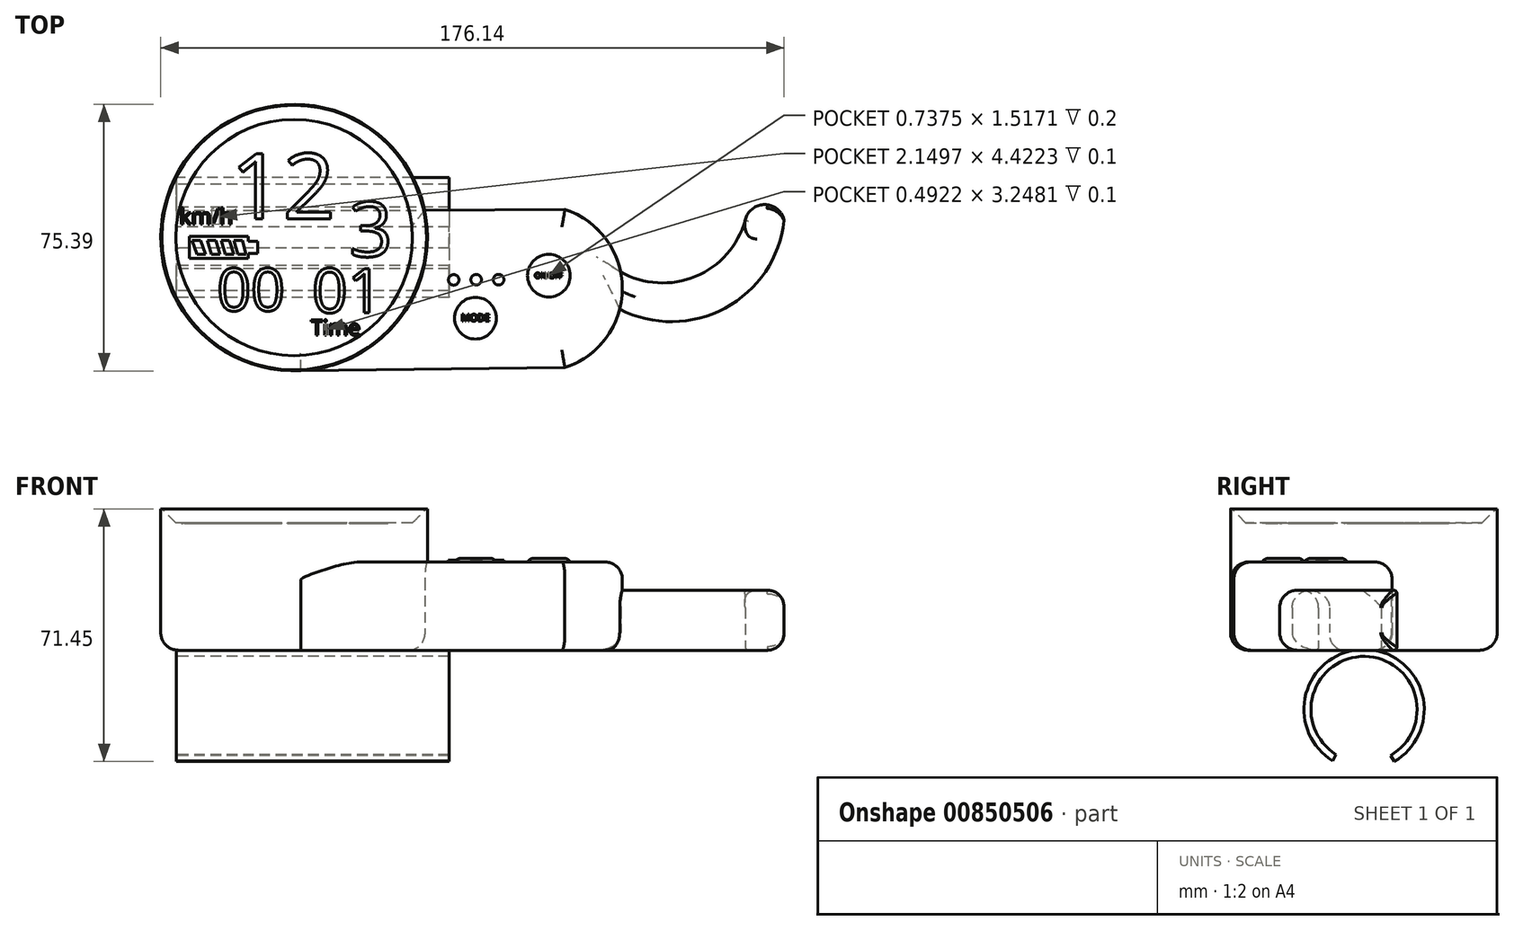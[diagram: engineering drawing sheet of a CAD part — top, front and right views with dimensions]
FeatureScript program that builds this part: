
annotation { "Feature Type Name" : "Feature", "Feature Type Description" : "" }
export const myFeature = defineFeature(function(context is Context, id is Id, definition is map)
    precondition{}
    {
        {
            var Q0;
            Q0=qCreatedBy(makeId("Top.planeOp"),FACE);
            var sketch = newSketch(context, id + "F0", { "sketchPlane" : qUnion([Q0])});
            skCircle(sketch, "E0", {"center": v(-18.77, 14.41) * mm, "radius": 37.7 * mm});
            skLineSegment(sketch, "E1", {"start": v(18.12, 22.13) * mm, "end": v(57.74, 22.38) * mm});
            skLineSegment(sketch, "E2.MirrorCS", {"start": v(-16.84, -23.23) * mm, "end": v(57.74, -22.38) * mm});
            skArc(sketch, "E3", {"start": v(57.74, -22.38) * mm, "mid": v(73.97, 0) * mm, "end": v(57.74, 22.38) * mm});
            skArc(sketch, "E4", {"start": v(73.5, 4.7) * mm, "mid": v(94.66, 3.43) * mm, "end": v(108.69, 19.33) * mm});
            skArc(sketch, "E5", {"start": v(73.23, -5.85) * mm, "mid": v(103.1, -5.5) * mm, "end": v(119.68, 19.33) * mm});
            skArc(sketch, "E6", {"start": v(119.68, 19.33) * mm, "mid": v(114.19, 23.75) * mm, "end": v(108.69, 19.33) * mm});
            skCircle(sketch, "E7", {"center": v(-18.77, 14.41) * mm, "radius": 32.4 * mm});
            skSolve(sketch);
        }
        {
            var Q0;
            {var subQ0=sQuery(id+"F0.wireOp",EDGE,"E0");var subQ1=makeQuery(id+"F0.imprint","INTERSECT",VERTEX,{"derivedFrom":[subQ0,sQuery(id+"F0.wireOp",EDGE,"E1")]});Q0=makeQuery(id+"F0.imprint","IMPRINT",FACE,{"disambiguationData":[TD([[makeQuery(id+"F0.imprint","IMPRINT",EDGE,{"disambiguationData":[TD([[subQ1,-1.0]])],"derivedFrom":subQ0}),1.0]])]});}
            extrude(context, id + "F1", {"entities" : qUnion([Q0]), "depth" : 40 * mm, "offsetDistance" : 25 * mm});
        }
        {
            var Q0;
            {var subQ3=sQuery(id+"F0.wireOp",EDGE,"E1");Q0=makeQuery(id+"F0.imprint","IMPRINT",FACE,{"disambiguationData":[TD([[makeQuery(id+"F0.imprint","IMPRINT",EDGE,{"derivedFrom":subQ3}),-1.0]])]});}
            extrude(context, id + "F2", {"entities" : qUnion([Q0]), "operationType" : NewBodyOperationType.ADD, "depth" : 25 * mm, "offsetDistance" : 25 * mm});
        }
        {
            var Q0;
            {var subQ0=sQuery(id+"F0.wireOp",EDGE,"E4");Q0=makeQuery(id+"F0.imprint","IMPRINT",FACE,{"disambiguationData":[TD([[makeQuery(id+"F0.imprint","IMPRINT",EDGE,{"derivedFrom":subQ0}),-1.0]])]});}
            extrude(context, id + "F3", {"entities" : qUnion([Q0]), "operationType" : NewBodyOperationType.ADD, "depth" : 17 * mm, "offsetDistance" : 25 * mm});
        }
        {
            var Q0;
            Q0=makeQuery(id+"F3.opExtrude","CAP_EDGE",EDGE,{"disambiguationData":[OSD([sQuery(id+"F0.wireOp",EDGE,"E5")])],"isStart":true});
            var Q1;
            Q1=makeQuery(id+"F3.opExtrude","CAP_EDGE",EDGE,{"disambiguationData":[OSD([sQuery(id+"F0.wireOp",EDGE,"E4")])],"isStart":false});
            var Q2;
            Q2=makeQuery(id+"F3.opExtrude","CAP_EDGE",EDGE,{"disambiguationData":[OSD([sQuery(id+"F0.wireOp",EDGE,"E5")])],"isStart":false});
            fillet(context, id + "F4", {"entities" : qUnion([Q0, Q1, Q2]), "radius" : 5 * mm, "tangentPropagation" : true, "allowEdgeOverflow" : false});
        }
        {
            var Q0;
            Q0=makeQuery(id+"F3.opExtrude","CAP_EDGE",EDGE,{"disambiguationData":[OSD([sQuery(id+"F0.wireOp",EDGE,"E6")])],"isStart":false});
            var Q1;
            Q1=makeQuery(id+"F4.opFillet","BLEND_EDGE",EDGE,{"blendedFrom":[makeQuery(id+"F3.opExtrude","CAP_EDGE",EDGE,{"disambiguationData":[OSD([sQuery(id+"F0.wireOp",EDGE,"E5")])],"isStart":false}),makeQuery(id+"F3.opExtrude","SWEPT_FACE",FACE,{"disambiguationData":[OSD([sQuery(id+"F0.wireOp",EDGE,"E6")])]})],"blendedInto":[makeQuery(id+"F3.opExtrude","SWEPT_FACE",FACE,{"disambiguationData":[OSD([sQuery(id+"F0.wireOp",EDGE,"E6")])]})]});
            fillet(context, id + "F5", {"entities" : qUnion([Q0, Q1]), "radius" : 1 * mm, "tangentPropagation" : true, "allowEdgeOverflow" : false});
        }
        {
            var Q0;
            Q0=makeQuery(id+"F2.opExtrude","CAP_EDGE",EDGE,{"disambiguationData":[OSD([sQuery(id+"F0.wireOp",EDGE,"E2.MirrorCS")])],"isStart":false});
            var Q1;
            Q1=makeQuery(id+"F2.opExtrude","CAP_EDGE",EDGE,{"disambiguationData":[OSD([sQuery(id+"F0.wireOp",EDGE,"E1")])],"isStart":false});
            var Q2;
            Q2=makeQuery(id+"F2.opExtrude","CAP_EDGE",EDGE,{"disambiguationData":[OSD([sQuery(id+"F0.wireOp",EDGE,"E2.MirrorCS")])],"isStart":true});
            var Q3;
            Q3=makeQuery(id+"F2.opExtrude","CAP_EDGE",EDGE,{"disambiguationData":[OSD([sQuery(id+"F0.wireOp",EDGE,"E1")])],"isStart":true});
            var Q4;
            {var subQ0=sQuery(id+"F0.wireOp",EDGE,"E1");var subQ1=sQuery(id+"F0.wireOp",EDGE,"E3");Q4=makeQuery(id+"F3.boolean.opBoolean","SPLIT",EDGE,{"disambiguationData":[TD([makeQuery(id+"F2.opExtrude","SWEPT_FACE",FACE,{"disambiguationData":[OSD([subQ0])]})])],"derivedFrom":makeQuery(id+"F2.opExtrude","CAP_EDGE",EDGE,{"disambiguationData":[OSD([subQ1])],"isStart":true})});}
            var Q5;
            {var subQ0=sQuery(id+"F0.wireOp",EDGE,"E2.MirrorCS");var subQ1=sQuery(id+"F0.wireOp",EDGE,"E3");Q5=makeQuery(id+"F3.boolean.opBoolean","SPLIT",EDGE,{"disambiguationData":[TD([makeQuery(id+"F2.opExtrude","SWEPT_FACE",FACE,{"disambiguationData":[OSD([subQ0])]})])],"derivedFrom":makeQuery(id+"F2.opExtrude","CAP_EDGE",EDGE,{"disambiguationData":[OSD([subQ1])],"isStart":true})});}
            var Q6;
            Q6=makeQuery(id+"F2.opExtrude","CAP_EDGE",EDGE,{"disambiguationData":[OSD([sQuery(id+"F0.wireOp",EDGE,"E3")])],"isStart":false});
            fillet(context, id + "F6", {"entities" : qUnion([Q0, Q1, Q2, Q3, Q4, Q5, Q6]), "radius" : 5 * mm, "tangentPropagation" : true, "allowEdgeOverflow" : false});
        }
        {
            var Q0;
            Q0=makeQuery(id+"F0.imprint","IMPRINT",FACE,{"disambiguationData":[TD([[makeQuery(id+"F0.imprint","IMPRINT",EDGE,{"derivedFrom":sQuery(id+"F0.wireOp",EDGE,"E7")}),1.0]])]});
            extrude(context, id + "F7", {"entities" : qUnion([Q0]), "operationType" : NewBodyOperationType.ADD, "depth" : 36 * mm, "offsetDistance" : 25 * mm});
        }
        {
            var Q0;
            Q0=makeQuery(id+"F1.opExtrude","CAP_EDGE",EDGE,{"disambiguationData":[OSD([sQuery(id+"F0.wireOp",EDGE,"E7")])],"isStart":false});
            chamfer(context, id + "F8", {"entities" : qUnion([Q0]), "width" : 5 * mm, "tangentPropagation" : true});
        }
        {
            var Q0;
            Q0=makeQuery(id+"F2.opExtrude","CAP_FACE",FACE,{"disambiguationData":[OSD([sQuery(id+"F0.wireOp",EDGE,"E0"),sQuery(id+"F0.wireOp",EDGE,"E1"),sQuery(id+"F0.wireOp",EDGE,"E2.MirrorCS"),sQuery(id+"F0.wireOp",EDGE,"E3")])],"isStart":false});
            var sketch = newSketch(context, id + "F9", { "sketchPlane" : qUnion([Q0])});
            skCircle(sketch, "E8", {"center": v(53.21, 3.66) * mm, "radius": 6.03 * mm});
            skCircle(sketch, "E9", {"center": v(32.47, -8.4) * mm, "radius": 5.9 * mm});
            skCircle(sketch, "E10", {"center": v(26.31, 2.45) * mm, "radius": 1.5 * mm});
            skCircle(sketch, "E11", {"center": v(32.67, 2.5) * mm, "radius": 1.5 * mm});
            skCircle(sketch, "E12", {"center": v(39, 2.52) * mm, "radius": 1.5 * mm});
            skSolve(sketch);
        }
        {
            var Q0;
            Q0=makeQuery(id+"F9.imprint","IMPRINT",FACE,{"disambiguationData":[TD([[makeQuery(id+"F9.imprint","IMPRINT",EDGE,{"derivedFrom":sQuery(id+"F9.wireOp",EDGE,"E9")}),1.0]])]});
            var Q1;
            Q1=makeQuery(id+"F9.imprint","IMPRINT",FACE,{"disambiguationData":[TD([[makeQuery(id+"F9.imprint","IMPRINT",EDGE,{"derivedFrom":sQuery(id+"F9.wireOp",EDGE,"E8")}),1.0]])]});
            extrude(context, id + "F10", {"entities" : qUnion([Q0, Q1]), "operationType" : NewBodyOperationType.ADD, "depth" : 1 * mm, "offsetDistance" : 25 * mm});
        }
        {
            var Q0;
            Q0=makeQuery(id+"F10.opExtrude","CAP_FACE",FACE,{"disambiguationData":[OSD([sQuery(id+"F9.wireOp",EDGE,"E9")])],"isStart":false});
            var Q1;
            Q1=makeQuery(id+"F10.opExtrude","CAP_FACE",FACE,{"disambiguationData":[OSD([sQuery(id+"F9.wireOp",EDGE,"E8")])],"isStart":false});
            fillet(context, id + "F11", {"entities" : qUnion([Q0, Q1]), "radius" : 2 * mm, "tangentPropagation" : true, "allowEdgeOverflow" : false});
        }
        {
            var Q0;
            Q0=makeQuery(id+"F9.imprint","IMPRINT",FACE,{"disambiguationData":[TD([[makeQuery(id+"F9.imprint","IMPRINT",EDGE,{"derivedFrom":sQuery(id+"F9.wireOp",EDGE,"E10")}),1.0]])]});
            var Q1;
            Q1=makeQuery(id+"F9.imprint","IMPRINT",FACE,{"disambiguationData":[TD([[makeQuery(id+"F9.imprint","IMPRINT",EDGE,{"derivedFrom":sQuery(id+"F9.wireOp",EDGE,"E11")}),1.0]])]});
            var Q2;
            Q2=makeQuery(id+"F9.imprint","IMPRINT",FACE,{"disambiguationData":[TD([[makeQuery(id+"F9.imprint","IMPRINT",EDGE,{"derivedFrom":sQuery(id+"F9.wireOp",EDGE,"E12")}),1.0]])]});
            extrude(context, id + "F12", {"entities" : qUnion([Q0, Q1, Q2]), "depth" : 0.5 * mm, "offsetDistance" : 25 * mm});
        }
        {
            var Q0;
            Q0=makeQuery(id+"F10.opExtrude","CAP_FACE",FACE,{"disambiguationData":[OSD([sQuery(id+"F9.wireOp",EDGE,"E9")])],"isStart":false});
            var sketch = newSketch(context, id + "F13", { "sketchPlane" : qUnion([Q0])});
            skText(sketch, "E13", { "text": "MODE", "fontName": "OpenSans-Regular.ttf"});
            skText(sketch, "E14", { "text": "ON/OFF", "fontName": "OpenSans-Regular.ttf"});
            const initialGuessF13  = {"E13": [0.02846, -0.00922, 1, 0, 0.00196], "E14": [0.0492, 0.00292, 1, 0, 0.00153]};
            skSetInitialGuess(sketch, initialGuessF13);
            skSolve(sketch);
        }
        {
            var Q0;
            Q0 = qSketchRegion(id + "F13", true);
            extrude(context, id + "F14", {"entities" : qUnion([Q0]), "operationType" : NewBodyOperationType.REMOVE, "oppositeDirection" : true, "depth" : 0.2 * mm, "offsetDistance" : 25 * mm});
        }
        {
            var Q0;
            Q0=makeQuery(id+"F1.opExtrude","CAP_EDGE",EDGE,{"disambiguationData":[OSD([sQuery(id+"F0.wireOp",EDGE,"E0")])],"isStart":true});
            fillet(context, id + "F15", {"entities" : qUnion([Q0]), "radius" : 5 * mm, "tangentPropagation" : true, "allowEdgeOverflow" : false});
        }
        {
            var Q0;
            Q0=makeQuery(id+"F7.opExtrude","CAP_FACE",FACE,{"disambiguationData":[OSD([sQuery(id+"F0.wireOp",EDGE,"E7")])],"isStart":false});
            var sketch = newSketch(context, id + "F16", { "sketchPlane" : qUnion([Q0])});
            skText(sketch, "E15", { "text": "12", "fontName": "OpenSans-Regular.ttf"});
            skText(sketch, "E16", { "text": "3", "fontName": "OpenSans-Regular.ttf"});
            skText(sketch, "E17", { "text": "01", "fontName": "OpenSans-Regular.ttf"});
            skText(sketch, "E18", { "text": "Time", "fontName": "OpenSans-Regular.ttf"});
            skText(sketch, "E19", { "text": "00", "fontName": "OpenSans-Regular.ttf"});
            skText(sketch, "E20", { "text": "km/h", "fontName": "OpenSans-Regular.ttf"});
            skLineSegment(sketch, "E21.bottom", {"start": v(-48.41, 14.72) * mm, "end": v(-31.8, 14.72) * mm});
            skLineSegment(sketch, "E21.top", {"start": v(-48.41, 8.5) * mm, "end": v(-31.8, 8.5) * mm});
            skLineSegment(sketch, "E21.left", {"start": v(-48.41, 14.72) * mm, "end": v(-48.41, 8.5) * mm});
            skLineSegment(sketch, "E21.right", {"start": v(-31.8, 14.72) * mm, "end": v(-31.8, 8.5) * mm});
            skLineSegment(sketch, "E22.bottom", {"start": v(-31.8, 13.4) * mm, "end": v(-29.04, 13.4) * mm});
            skLineSegment(sketch, "E22.top", {"start": v(-31.8, 9.88) * mm, "end": v(-29.04, 9.88) * mm});
            skLineSegment(sketch, "E22.left", {"start": v(-31.8, 11.61) * mm, "end": v(-31.8, 9.88) * mm});
            skLineSegment(sketch, "E22.right", {"start": v(-29.04, 13.4) * mm, "end": v(-29.04, 9.88) * mm});
            skLineSegment(sketch, "E23", {"start": v(-47.58, 13.64) * mm, "end": v(-45.18, 13.64) * mm});
            skLineSegment(sketch, "E24", {"start": v(-45.18, 13.64) * mm, "end": v(-43.77, 9.64) * mm});
            skLineSegment(sketch, "E25", {"start": v(-43.77, 9.64) * mm, "end": v(-46.17, 9.64) * mm});
            skLineSegment(sketch, "E26", {"start": v(-46.17, 9.64) * mm, "end": v(-47.58, 13.64) * mm});
            skLineSegment(sketch, "E27", {"start": v(-43.3, 13.65) * mm, "end": v(-40.9, 13.65) * mm});
            skLineSegment(sketch, "E28", {"start": v(-40.9, 13.65) * mm, "end": v(-39.78, 9.65) * mm});
            skLineSegment(sketch, "E29", {"start": v(-39.78, 9.65) * mm, "end": v(-42.18, 9.65) * mm});
            skLineSegment(sketch, "E30", {"start": v(-42.18, 9.65) * mm, "end": v(-43.3, 13.65) * mm});
            skLineSegment(sketch, "E31", {"start": v(-39.42, 13.65) * mm, "end": v(-37.02, 13.65) * mm});
            skLineSegment(sketch, "E32", {"start": v(-37.02, 13.65) * mm, "end": v(-35.86, 9.65) * mm});
            skLineSegment(sketch, "E33", {"start": v(-35.86, 9.65) * mm, "end": v(-38.26, 9.65) * mm});
            skLineSegment(sketch, "E34", {"start": v(-38.26, 9.65) * mm, "end": v(-39.42, 13.65) * mm});
            skLineSegment(sketch, "E35", {"start": v(-35.77, 13.65) * mm, "end": v(-33.37, 13.65) * mm});
            skLineSegment(sketch, "E36", {"start": v(-33.37, 13.65) * mm, "end": v(-32.32, 9.65) * mm});
            skLineSegment(sketch, "E37", {"start": v(-32.32, 9.65) * mm, "end": v(-34.72, 9.65) * mm});
            skLineSegment(sketch, "E38", {"start": v(-34.72, 9.65) * mm, "end": v(-35.77, 13.65) * mm});
            const initialGuessF16  = {"E15": [-0.03673, 0.01965, 1, 0, 0.01863], "E16": [-0.0033, 0.00906, 1, 0, 0.01552], "E17": [-0.01372, -0.00683, 1, 0, 0.0126], "E18": [-0.01403, -0.01321, 1, 0, 0.00437], "E19": [-0.04056, -0.00628, 1, 0, 0.01205], "E20": [-0.05115, 0.01817, 1, 0, 0.00446]};
            skSetInitialGuess(sketch, initialGuessF16);
            skSolve(sketch);
        }
        {
            var Q0;
            {var subQ1=sQuery(id+"F16.wireOp",EDGE,"E22.bottom");Q0=makeQuery(id+"F16.imprint","IMPRINT",FACE,{"disambiguationData":[TD([[makeQuery(id+"F16.imprint","IMPRINT",EDGE,{"derivedFrom":subQ1}),-1.0]])]});}
            var Q1;
            {var subQ4=sQuery(id+"F16.wireOp",EDGE,"E21.bottom");Q1=makeQuery(id+"F16.imprint","IMPRINT",FACE,{"disambiguationData":[TD([[makeQuery(id+"F16.imprint","IMPRINT",EDGE,{"derivedFrom":subQ4}),-1.0]])]});}
            var Q2;
            Q2=makeQuery(id+"F16.imprint","IMPRINT",FACE,{"disambiguationData":[TD([[makeQuery(id+"F16.imprint","IMPRINT",EDGE,{"derivedFrom":sQuery(id+"F16.wireOp",EDGE,"E16.sketch_text.stroke-0")}),-1.0]])]});
            var Q3;
            Q3=makeQuery(id+"F16.imprint","IMPRINT",FACE,{"disambiguationData":[TD([[makeQuery(id+"F16.imprint","IMPRINT",EDGE,{"derivedFrom":sQuery(id+"F16.wireOp",EDGE,"E17.sketch_text.stroke-16")}),-1.0]])]});
            var Q4;
            Q4=makeQuery(id+"F16.imprint","IMPRINT",FACE,{"disambiguationData":[TD([[makeQuery(id+"F16.imprint","IMPRINT",EDGE,{"derivedFrom":sQuery(id+"F16.wireOp",EDGE,"E17.sketch_text.stroke-0")}),-1.0]])]});
            var Q5;
            Q5=makeQuery(id+"F16.imprint","IMPRINT",FACE,{"disambiguationData":[TD([[makeQuery(id+"F16.imprint","IMPRINT",EDGE,{"derivedFrom":sQuery(id+"F16.wireOp",EDGE,"E18.sketch_text.stroke-0")}),-1.0]])]});
            var Q6;
            Q6=makeQuery(id+"F16.imprint","IMPRINT",FACE,{"disambiguationData":[TD([[makeQuery(id+"F16.imprint","IMPRINT",EDGE,{"derivedFrom":sQuery(id+"F16.wireOp",EDGE,"E18.sketch_text.stroke-12")}),-1.0]])]});
            var Q7;
            Q7=makeQuery(id+"F16.imprint","IMPRINT",FACE,{"disambiguationData":[TD([[makeQuery(id+"F16.imprint","IMPRINT",EDGE,{"derivedFrom":sQuery(id+"F16.wireOp",EDGE,"E18.sketch_text.stroke-8")}),-1.0]])]});
            var Q8;
            Q8=makeQuery(id+"F16.imprint","IMPRINT",FACE,{"disambiguationData":[TD([[makeQuery(id+"F16.imprint","IMPRINT",EDGE,{"derivedFrom":sQuery(id+"F16.wireOp",EDGE,"E18.sketch_text.stroke-20")}),-1.0]])]});
            var Q9;
            Q9=makeQuery(id+"F16.imprint","IMPRINT",FACE,{"disambiguationData":[TD([[makeQuery(id+"F16.imprint","IMPRINT",EDGE,{"derivedFrom":sQuery(id+"F16.wireOp",EDGE,"E18.sketch_text.stroke-48")}),-1.0]])]});
            var Q10;
            Q10=makeQuery(id+"F16.imprint","IMPRINT",FACE,{"disambiguationData":[TD([[makeQuery(id+"F16.imprint","IMPRINT",EDGE,{"derivedFrom":sQuery(id+"F16.wireOp",EDGE,"E19.sketch_text.stroke-16")}),-1.0]])]});
            var Q11;
            Q11=makeQuery(id+"F16.imprint","IMPRINT",FACE,{"disambiguationData":[TD([[makeQuery(id+"F16.imprint","IMPRINT",EDGE,{"derivedFrom":sQuery(id+"F16.wireOp",EDGE,"E19.sketch_text.stroke-0")}),-1.0]])]});
            var Q12;
            Q12=makeQuery(id+"F16.imprint","IMPRINT",FACE,{"disambiguationData":[TD([[makeQuery(id+"F16.imprint","IMPRINT",EDGE,{"derivedFrom":sQuery(id+"F16.wireOp",EDGE,"E15.sketch_text.stroke-9")}),-1.0]])]});
            var Q13;
            Q13=makeQuery(id+"F16.imprint","IMPRINT",FACE,{"disambiguationData":[TD([[makeQuery(id+"F16.imprint","IMPRINT",EDGE,{"derivedFrom":sQuery(id+"F16.wireOp",EDGE,"E15.sketch_text.stroke-0")}),-1.0]])]});
            var Q14;
            Q14=makeQuery(id+"F16.imprint","IMPRINT",FACE,{"disambiguationData":[TD([[makeQuery(id+"F16.imprint","IMPRINT",EDGE,{"derivedFrom":sQuery(id+"F16.wireOp",EDGE,"E20.sketch_text.stroke-15")}),-1.0]])]});
            var Q15;
            Q15=makeQuery(id+"F16.imprint","IMPRINT",FACE,{"disambiguationData":[TD([[makeQuery(id+"F16.imprint","IMPRINT",EDGE,{"derivedFrom":sQuery(id+"F16.wireOp",EDGE,"E20.sketch_text.stroke-43")}),-1.0]])]});
            var Q16;
            Q16=makeQuery(id+"F16.imprint","IMPRINT",FACE,{"disambiguationData":[TD([[makeQuery(id+"F16.imprint","IMPRINT",EDGE,{"derivedFrom":sQuery(id+"F16.wireOp",EDGE,"E20.sketch_text.stroke-47")}),-1.0]])]});
            var Q17;
            Q17=makeQuery(id+"F16.imprint","IMPRINT",FACE,{"disambiguationData":[TD([[makeQuery(id+"F16.imprint","IMPRINT",EDGE,{"derivedFrom":sQuery(id+"F16.wireOp",EDGE,"E20.sketch_text.stroke-0")}),-1.0]])]});
            extrude(context, id + "F17", {"entities" : qUnion([Q0, Q1, Q2, Q3, Q4, Q5, Q6, Q7, Q8, Q9, Q10, Q11, Q12, Q13, Q14, Q15, Q16, Q17]), "operationType" : NewBodyOperationType.REMOVE, "oppositeDirection" : true, "depth" : 0.1 * mm, "offsetDistance" : 25 * mm});
        }
        {
            var Q0;
            Q0=qCreatedBy(makeId("Right.planeOp"),FACE);
            var sketch = newSketch(context, id + "F18", { "sketchPlane" : qUnion([Q0])});
            skArc(sketch, "E39", {"start": v(21.96, -29.73) * mm, "mid": v(14.7, -1.74) * mm, "end": v(6.53, -29.48) * mm});
            skArc(sketch, "E40.0", {"start": v(22.97, -31.45) * mm, "mid": v(14.66, 0.26) * mm, "end": v(5.58, -31.24) * mm});
            skLineSegment(sketch, "E41", {"start": v(21.96, -29.73) * mm, "end": v(22.97, -31.45) * mm});
            skLineSegment(sketch, "E42", {"start": v(6.53, -29.48) * mm, "end": v(5.58, -31.24) * mm});
            skSolve(sketch);
        }
        {
            var Q0;
            Q0=makeQuery(id+"F18.imprint","IMPRINT",FACE,{"disambiguationData":[TD([[makeQuery(id+"F18.imprint","IMPRINT",EDGE,{"derivedFrom":sQuery(id+"F18.wireOp",EDGE,"E39")}),-1.0]])]});
            extrude(context, id + "F19", {"entities" : qUnion([Q0]), "operationType" : NewBodyOperationType.ADD, "depth" : 25 * mm, "offsetDistance" : 25 * mm, "hasSecondDirection" : true, "secondDirectionOppositeDirection" : true, "secondDirectionDepth" : 52 * mm});
        }
    });
